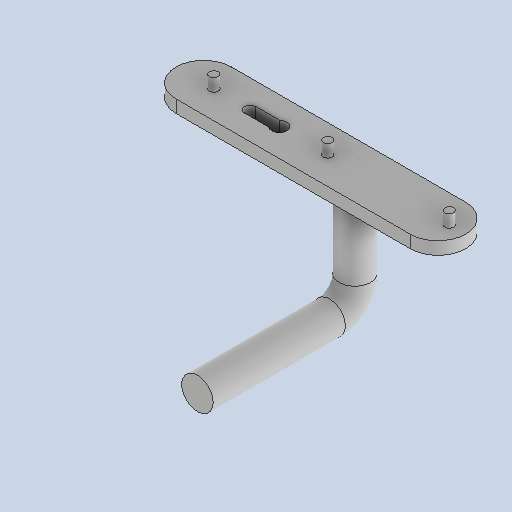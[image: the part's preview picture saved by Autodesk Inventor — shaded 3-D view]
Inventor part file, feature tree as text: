
AUTODESK INVENTOR PART (.ipt)
format: ipt  version: 2025.1 (Build 291241000, 241)  size: 134,144 bytes
history: native  units: mm
features: other x4, sketch x4, plane x1
ambient origin geometry x8: Origin, YZ Plane, XZ Plane, XY Plane, X Axis, Y Axis, Z Axis, Center Point
bodies: Body1 (feature_tree)
feature tree (9):
  other  "garnitur_lang_links.ipt"
  other  "Solid2::garnitur_lang_links.ipt"
  other  "TaggingFeature1"
  sketch  "Sketch1"  dims[d0=10.0mm]
  sketch  "Sketch2"
  sketch  "Sketch5"
  sketch  "Sketch6"
  plane  "Work Plane1"
  other  "Work Point1"
